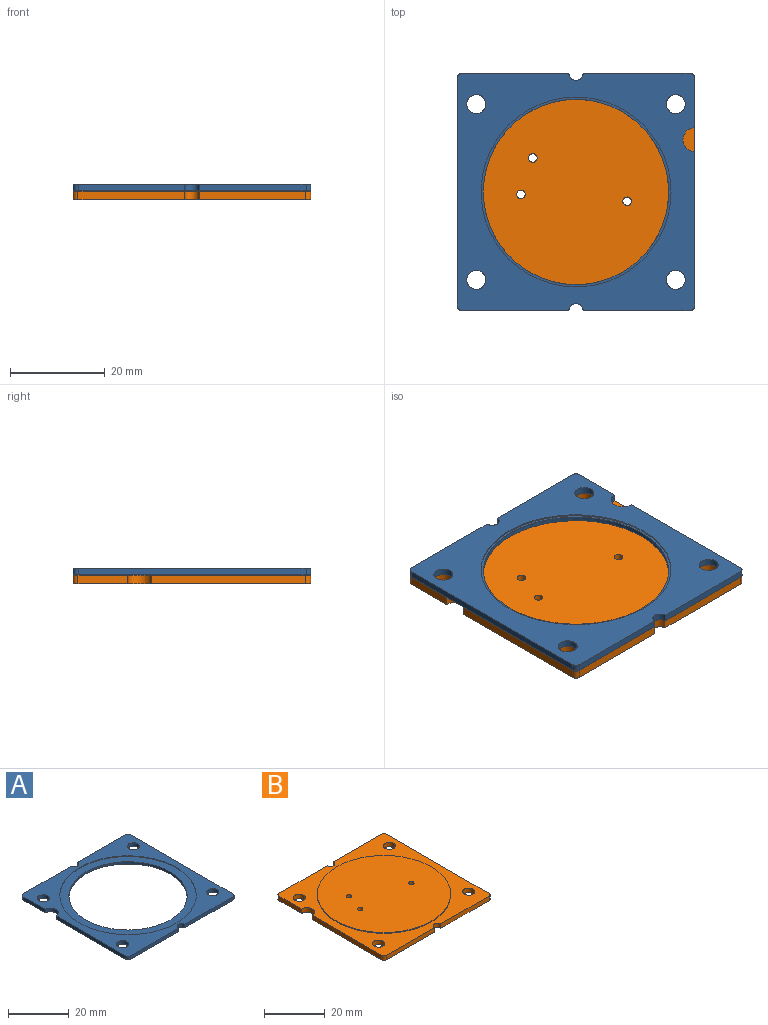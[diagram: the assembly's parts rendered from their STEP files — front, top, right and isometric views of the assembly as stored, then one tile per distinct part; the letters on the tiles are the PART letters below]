
ASSEMBLY  parts=2 mates=1
PART A: 25 faces, bbox 50x50x1.4 mm
  f0: cylinder r=1.5mm len=3mm, axis (0,0,-1), area 6.6mm2, adj f1,f16,f18,f19
  f1: plane 22.5x1.4mm, normal (0,-1,0), area 31.5mm2, adj f0,f2,f18,f19
  f2: cylinder r=1mm len=1.4mm, axis (0,0,-1), area 2.2mm2, adj f1,f3,f18,f19
  f3: plane 48x1.4mm, normal (1,0,0), area 67.2mm2, adj f2,f4,f18,f19
  f4: cylinder r=1mm len=1.4mm, axis (0,0,-1), area 2.2mm2, adj f3,f5,f18,f19
  f5: plane 22.5x1.4mm, normal (0,1,0), area 31.5mm2, adj f4,f6,f18,f19
  f6: cylinder r=1.5mm len=3mm, axis (0,0,-1), area 6.6mm2, adj f5,f7,f18,f19
  f7: plane 22.5x1.4mm, normal (0,1,0), area 31.5mm2, adj f6,f8,f18,f19
  f8: cylinder r=1mm len=1.4mm, axis (0,0,-1), area 2.2mm2, adj f7,f9,f18,f19
  f9: plane 10.5x1.4mm, normal (-1,0,0), area 14.7mm2, adj f8,f10,f18,f19
  f10: cylinder r=2.5mm len=5mm, axis (0,0,-1), area 11mm2, adj f9,f11,f18,f19
  f11: plane 32.5x1.4mm, normal (-1,0,0), area 45.5mm2, adj f10,f12,f18,f19
  f12: cylinder r=1mm len=1.4mm, axis (0,0,-1), area 2.2mm2, adj f11,f16,f18,f19
  f13: cylinder r=2.01mm len=4.01mm, axis (0,0,-1), area 17.7mm2, adj f18,f19
  f14: cylinder r=2.01mm len=4.01mm, axis (0,0,-1), area 17.7mm2, adj f18,f19
  f15: cylinder r=2.01mm len=4.01mm, axis (0,0,-1), area 17.7mm2, adj f18,f19
  f16: plane 22.5x1.4mm, normal (0,-1,0), area 31.5mm2, adj f0,f12,f18,f19
  f17: cylinder r=2.01mm len=4.01mm, axis (0,0,-1), area 17.7mm2, adj f18,f19
  f18: plane 50x50mm, normal (0,0,1), area 841.2mm2, adj f0,f1,f2,f3,f4,f5,f6,f7
  f19: plane 50x50mm, normal (0,0,-1), area 1175mm2, adj f0,f1,f2,f3,f4,f5,f6,f7
  f20: cylinder r=22.5mm len=45mm, axis (0,0,1), area 35.3mm2, adj f18,f21
  f21: plane 45x45mm, normal (0,0,1), area 395.8mm2, adj f20,f24
  f22: cylinder r=20mm len=40mm, axis (0,0,-1), area 31.4mm2, adj f19,f23
  f23: plane 40x40mm, normal (0,0,-1), area 62mm2, adj f22,f24
  f24: cylinder r=19.5mm len=39mm, axis (0,0,1), area 110.3mm2, adj f21,f23
PART B: 25 faces, bbox 50x50x2.1 mm
  f0: cylinder r=22mm len=44mm, axis (0,0,-1), area 41.5mm2, adj f1,f20
  f1: plane 44x44mm, normal (0,0,1), area 1512.9mm2, adj f0,f22,f23,f24
  f2: plane 48x1.8mm, normal (1,0,0), area 86.4mm2, adj f3,f19,f20,f21
  f3: cylinder r=1mm len=1.8mm, axis (0,0,-1), area 2.8mm2, adj f2,f4,f20,f21
  f4: plane 22.5x1.8mm, normal (0,1,0), area 40.5mm2, adj f3,f5,f20,f21
  f5: cylinder r=1.5mm len=3mm, axis (0,0,-1), area 8.5mm2, adj f4,f6,f20,f21
  f6: plane 22.5x1.8mm, normal (0,1,0), area 40.5mm2, adj f5,f7,f20,f21
  f7: cylinder r=1mm len=1.8mm, axis (0,0,-1), area 2.8mm2, adj f6,f8,f20,f21
  f8: plane 10.5x1.8mm, normal (-1,0,0), area 18.9mm2, adj f7,f9,f20,f21
  f9: cylinder r=2.5mm len=5mm, axis (0,0,-1), area 14.1mm2, adj f8,f10,f20,f21
  f10: plane 32.5x1.8mm, normal (-1,0,0), area 58.5mm2, adj f9,f11,f20,f21
  f11: cylinder r=1mm len=1.8mm, axis (0,0,-1), area 2.8mm2, adj f10,f12,f20,f21
  f12: plane 22.5x1.8mm, normal (0,-1,0), area 40.5mm2, adj f11,f13,f20,f21
  f13: cylinder r=1.5mm len=3mm, axis (0,0,-1), area 8.5mm2, adj f12,f14,f20,f21
  f14: plane 22.5x1.8mm, normal (0,-1,0), area 40.5mm2, adj f13,f19,f20,f21
  f15: cylinder r=2mm len=4.01mm, axis (0,0,-1), area 22.7mm2, adj f20,f21
  f16: cylinder r=2mm len=4.01mm, axis (0,0,-1), area 22.7mm2, adj f20,f21
  f17: cylinder r=2mm len=4.01mm, axis (0,0,-1), area 22.7mm2, adj f20,f21
  f18: cylinder r=2mm len=4.01mm, axis (0,0,-1), area 22.7mm2, adj f20,f21
  f19: cylinder r=1mm len=1.8mm, axis (0,0,-1), area 2.8mm2, adj f2,f14,f20,f21
  f20: plane 50x50mm, normal (0,0,1), area 911.2mm2, adj f0,f2,f3,f4,f5,f6,f7,f8
  f21: plane 50x50mm, normal (0,0,-1), area 2424.1mm2, adj f2,f3,f4,f5,f6,f7,f8,f9
  f22: cylinder r=0.9mm len=2.1mm, axis (0,0,1), area 11.9mm2, adj f1,f21
  f23: cylinder r=0.9mm len=2.1mm, axis (0,0,1), area 11.9mm2, adj f1,f21
  f24: cylinder r=0.9mm len=2.1mm, axis (0,0,1), area 11.9mm2, adj f1,f21
PLACE A rot(axis=(0,1,0),180deg) t=(0.02,-0.01,1.15)mm
PLACE B t=(0,0,-2.1)mm
MATE fastened B.f1 <-> A.f24  axis (0,0,1) through (0.02,-0.01,0)mm
